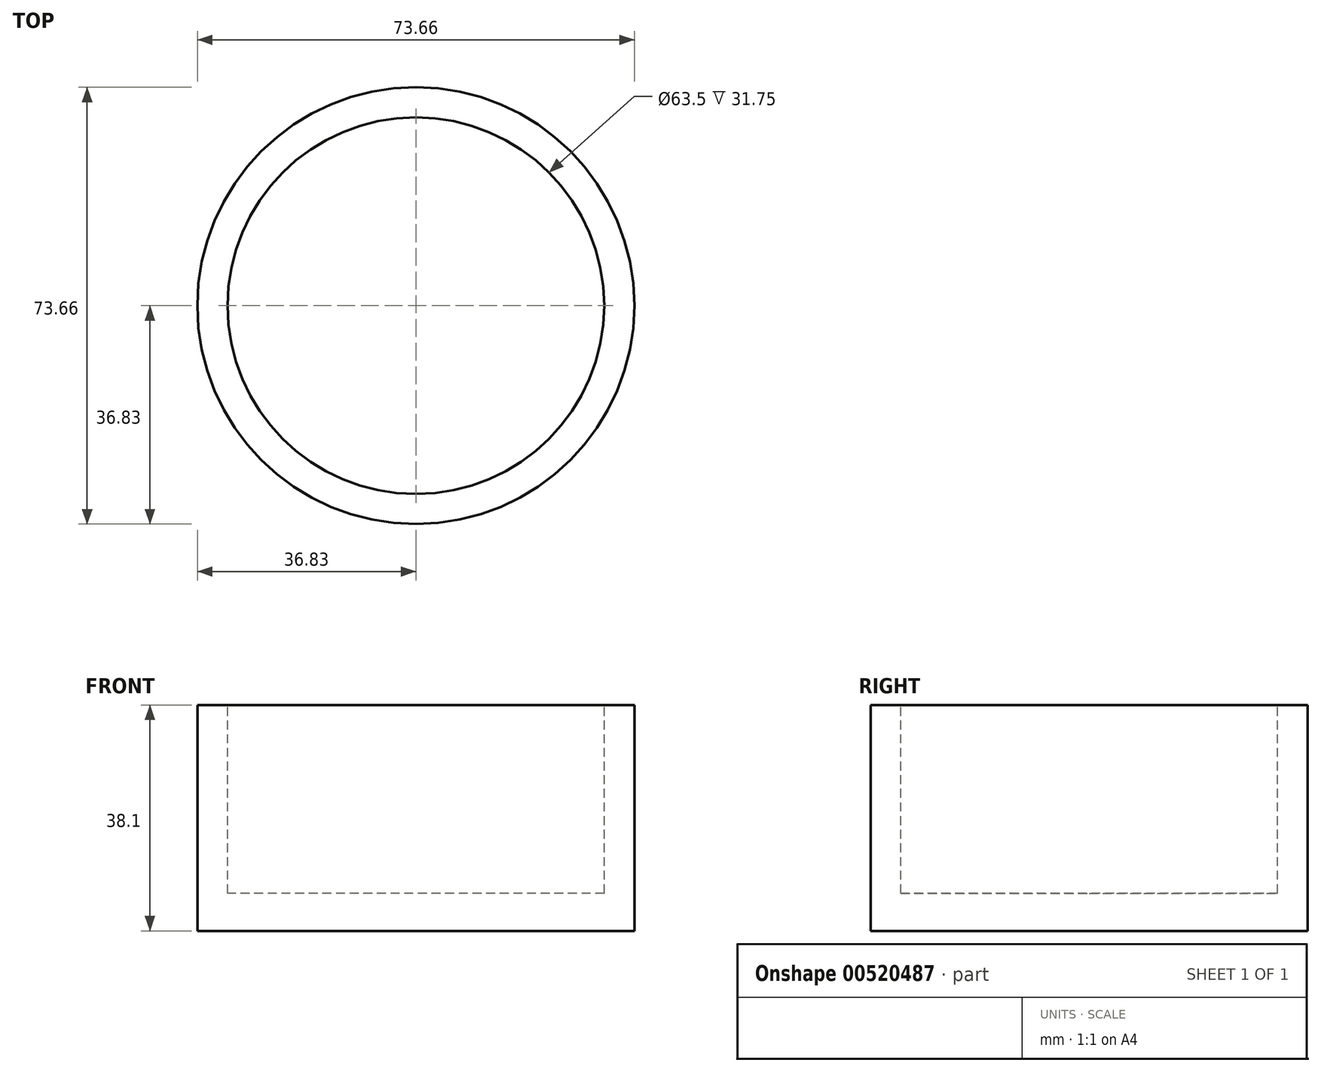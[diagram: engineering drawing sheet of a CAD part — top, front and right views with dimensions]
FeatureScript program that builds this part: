
annotation { "Feature Type Name" : "Feature", "Feature Type Description" : "" }
export const myFeature = defineFeature(function(context is Context, id is Id, definition is map)
    precondition{}
    {
        {
            var Q0;
            Q0=qCreatedBy(makeId("Top.planeOp"),FACE);
            var sketch = newSketch(context, id + "F0", { "sketchPlane" : qUnion([Q0])});
            skCircle(sketch, "E0", {"center": v(0, 0) * mm, "radius": 36.83 * mm});
            skSolve(sketch);
        }
        {
            var Q0;
            Q0 = qSketchRegion(id + "F0", true);
            extrude(context, id + "F1", {"entities" : qUnion([Q0]), "depth" : 38.1 * mm, "offsetDistance" : 25.4 * mm});
        }
        {
            var Q0;
            Q0=makeQuery(id+"F1.opExtrude","CAP_FACE",FACE,{"disambiguationData":[OSD([sQuery(id+"F0.wireOp",EDGE,"E0")])],"isStart":false});
            var sketch = newSketch(context, id + "F2", { "sketchPlane" : qUnion([Q0])});
            skCircle(sketch, "E1", {"center": v(0, 0) * mm, "radius": 31.75 * mm});
            skSolve(sketch);
        }
        {
            var Q0;
            Q0=makeQuery(id+"F2.imprint","IMPRINT",FACE,{"disambiguationData":[TD([[makeQuery(id+"F2.imprint","IMPRINT",EDGE,{"derivedFrom":sQuery(id+"F2.wireOp",EDGE,"E1")}),1.0]])]});
            extrude(context, id + "F3", {"entities" : qUnion([Q0]), "operationType" : NewBodyOperationType.REMOVE, "oppositeDirection" : true, "depth" : 31.75 * mm, "offsetDistance" : 25.4 * mm});
        }
    });
